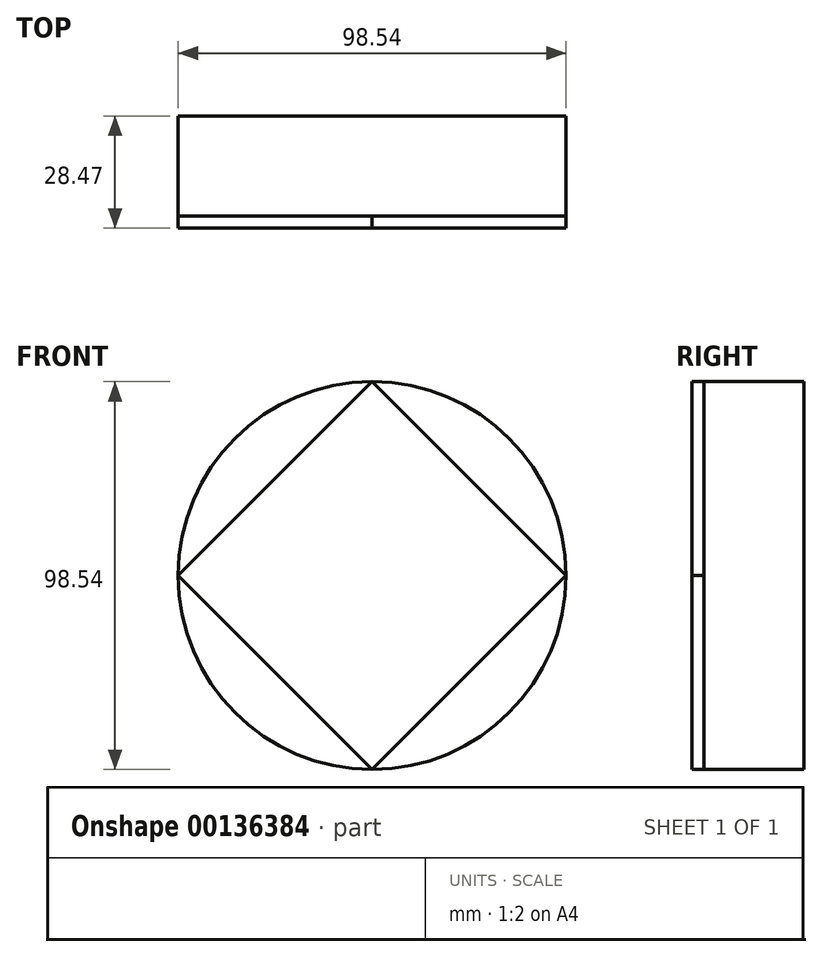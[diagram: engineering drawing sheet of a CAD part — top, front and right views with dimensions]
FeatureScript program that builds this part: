
annotation { "Feature Type Name" : "Feature", "Feature Type Description" : "" }
export const myFeature = defineFeature(function(context is Context, id is Id, definition is map)
    precondition{}
    {
        {
            var Q0;
            Q0=qCreatedBy(makeId("Front.planeOp"),FACE);
            var sketch = newSketch(context, id + "F0", { "sketchPlane" : qUnion([Q0])});
            skCircle(sketch, "E0", {"center": v(0, 0) * mm, "radius": 49.27 * mm});
            skSolve(sketch);
        }
        {
            var Q0;
            Q0=makeQuery(id+"F0.imprint","IMPRINT",FACE,{"disambiguationData":[TD([[makeQuery(id+"F0.imprint","IMPRINT",EDGE,{"derivedFrom":sQuery(id+"F0.wireOp",EDGE,"E0")}),1.0]])]});
            extrude(context, id + "F1", {"entities" : qUnion([Q0]), "depth" : 25.4 * mm});
        }
        {
            var Q0;
            Q0=makeQuery(id+"F1.opExtrude","CAP_FACE",FACE,{"disambiguationData":[OSD([sQuery(id+"F0.wireOp",EDGE,"E0")])],"isStart":false});
            var sketch = newSketch(context, id + "F2", { "sketchPlane" : qUnion([Q0])});
            skLineSegment(sketch, "E1", {"start": v(0, 49.27) * mm, "end": v(-49.27, 0) * mm});
            skLineSegment(sketch, "E2", {"start": v(-49.27, 0) * mm, "end": v(0, -49.27) * mm});
            skLineSegment(sketch, "E3", {"start": v(0, -49.27) * mm, "end": v(49.27, 0) * mm});
            skLineSegment(sketch, "E4", {"start": v(49.27, 0) * mm, "end": v(0, 49.27) * mm});
            skSolve(sketch);
        }
        {
            var Q0;
            Q0=makeQuery(id+"F2.imprint","IMPRINT",FACE,{"disambiguationData":[TD([[makeQuery(id+"F2.imprint","IMPRINT",EDGE,{"derivedFrom":sQuery(id+"F2.wireOp",EDGE,"E1")}),1.0]])]});
            extrude(context, id + "F3", {"entities" : qUnion([Q0]), "operationType" : NewBodyOperationType.ADD, "depth" : 3.07 * mm});
        }
    });
